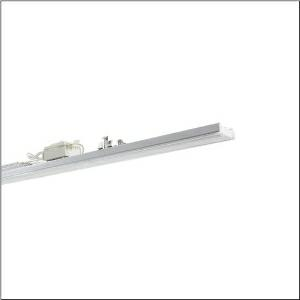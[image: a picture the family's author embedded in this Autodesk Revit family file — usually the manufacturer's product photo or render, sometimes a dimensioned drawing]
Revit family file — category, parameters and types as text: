
# Revit family: licross_21_recessed_mo_52te11dv4dxg
name_source: partatom
category: Lighting Fixtures
units: mm (PartAtom-declared; Revit-internal decimal feet)

## family parameters
Cut with Voids When Loaded = No
Host = Face
Light Source = No
Part Type = Normal
Room Calculation Point = No
Round Connector Dimension = Use Diameter
Shared = No

## types (1)
- --- (1 x LED, 13000 lm, 72.2 W, 4000K)
    Apparent Load = 72 VA
    CIE Flux Codes = 89 96 99 100 100
    Color Rendering = 80
    Color Temperature = 4000K
    Default Elevation = 1800 mm
    Description = Licross 21 Recessed MO, luminaire insert, of sheet steel, galvanised, coil coated, white, length: 2.250mm, width: 66mm, height: 67mm, LED rated luminous flux: 13.000lm, light colour: 840, SDCM (Standard Deviation of Colour Matching)MacAdam ≤ 3 SDCM (initial), control gear: DALI 2, with plug, 5-pole, with phase selection, mains connection: 220..240V, AC, 50/60Hz, rated input power: 72W, internal wiring halogen-free, primary light control with lens, of plastic, primary optical cover: cover, of PMMA, light emission: direct distribution, primary light characteristic: symmetric, protection rating (complete): IP54, insulation class (complete): insulation class I (protective earthing), certification: CE, ENEC, VDE, UKCA, protection symbol: D if used in an environment with non-conductive dust loads with corresponding accessories, impact resistance: IK06, permissible ambient temperature for indoor applications: -25..+35°C, corresponds to IFS (International Featured Standards) requirements for safety and quality in the food industry, reducing of maximum allowable ambient temperature of 5°C with ceiling mounting, LABS conformity tested according to VDMA 24364:2018-05, The light source and the operating device comply with the requirements of the Ecodesign Regulation (EU) 2019/2020 and are replaceable in accordance with this regulation, packaging unit: 1 piece
    Height = 58 mm
    Lamp = 1 x LED
    Lamp Light Flux = 13000 lm
    Lamp Power = 72.2 W
    Lamp count = 1
    Length = 2250 mm
    Luminous efficacy = 180 lm/W
    Manufacturer = Siteco
    ModVariant = No
    Model = 52TE11DV4DXG
    Mounting Place = Ceiling
    Mounting Type = Pendant
    Number of Poles = 1
    OnlyDefault = Yes
    Power Factor = 1
    Product Name = Licross 21 Recessed MO
    Product group = luminaire insert | ceiling pendant
    ProductGroupID = 901
    Protection Class = Protection class I
    Protection Degree = IP 54
    RLX_Detail_Level = 1
    RLX_Emergency_Light_Flux = 0 lm
    RLX_Emergency_Type = 0
    RLX_Emergency_Type_DB = No
    RlxData = <blob elided: 29845 chars, md5=0d5558b8>
    Socket = socket
    Standby Power = 0 W
    System Light Flux = 13000 lm
    System Power = 72 W
    Type Comments = factory setting: luminous flux: 100 % | dim-lin: 254 | 329 mA
    Type Image = l_1296930.jpg
    URL = http://relux.com
    VarID = @adj_127175
    Voltage = 0 V
    Weight = 0.00 kg
    Width = 66 mm

## geometry (parser evidence)
native form markers: Blend x4, Sweep x8
no freeform markers — native parametric forms only
